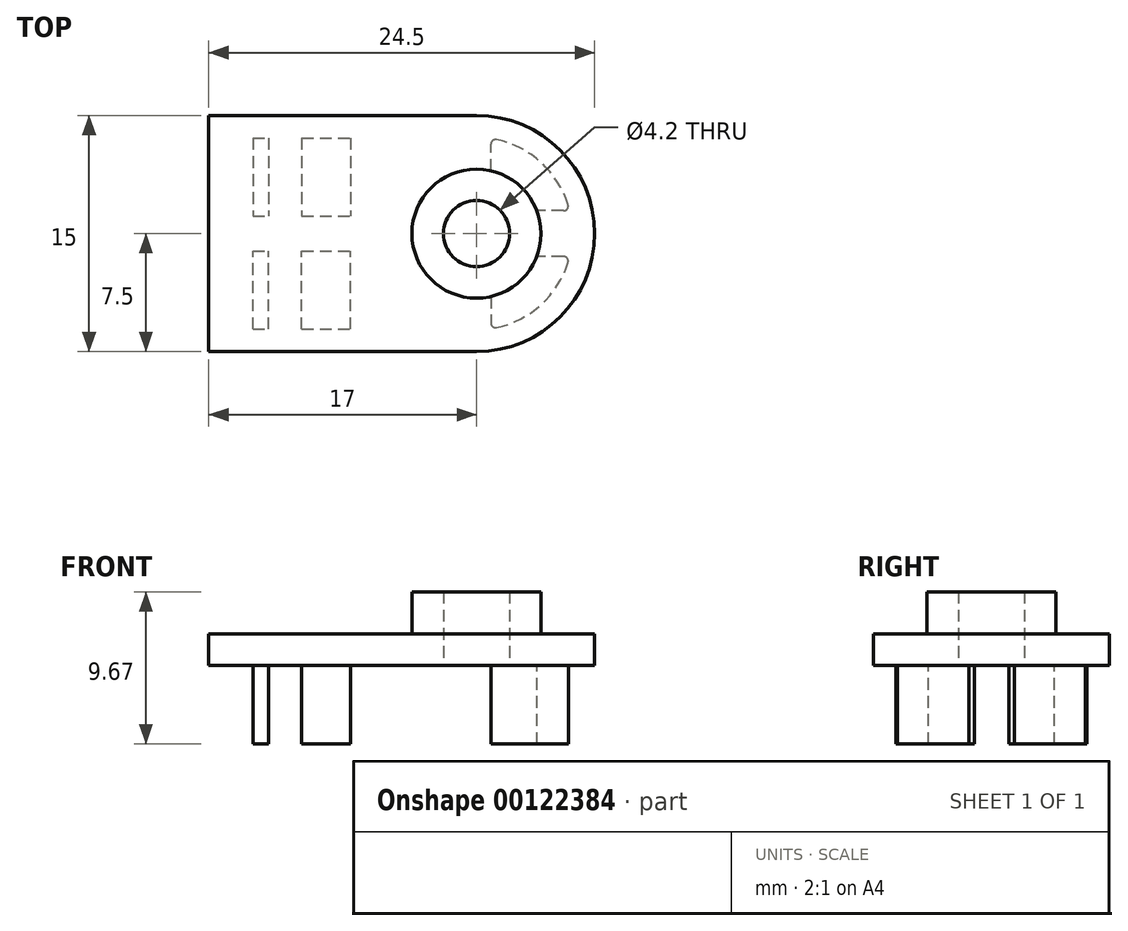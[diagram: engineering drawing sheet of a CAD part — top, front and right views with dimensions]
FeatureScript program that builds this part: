
annotation { "Feature Type Name" : "Feature", "Feature Type Description" : "" }
export const myFeature = defineFeature(function(context is Context, id is Id, definition is map)
    precondition{}
    {
        {
            var Q0;
            Q0=qCreatedBy(makeId("Top.planeOp"),FACE);
            var sketch = newSketch(context, id + "F0", { "sketchPlane" : qUnion([Q0])});
            skLineSegment(sketch, "E0.bottom", {"start": v(0, 0) * mm, "end": v(17, 0) * mm});
            skLineSegment(sketch, "E0.top", {"start": v(0, 15) * mm, "end": v(17, 15) * mm});
            skLineSegment(sketch, "E0.left", {"start": v(0, 0) * mm, "end": v(0, 15) * mm});
            skLineSegment(sketch, "E0.right", {"start": v(17, 0) * mm, "end": v(17, 15) * mm, "construction": true});
            skArc(sketch, "E1", {"start": v(17, 0) * mm, "mid": v(24.5, 7.5) * mm, "end": v(17, 15) * mm});
            skCircle(sketch, "E2", {"center": v(17, 7.5) * mm, "radius": 2.1 * mm});
            skSolve(sketch);
        }
        {
            var Q0;
            Q0 = qSketchRegion(id + "F0", true);
            extrude(context, id + "F1", {"entities" : qUnion([Q0]), "depth" : 2 * mm});
        }
        {
            var Q0;
            Q0=makeQuery(id+"F1.opExtrude","CAP_FACE",FACE,{"disambiguationData":[OSD([sQuery(id+"F0.wireOp",EDGE,"E0.bottom"),sQuery(id+"F0.wireOp",EDGE,"E0.top"),sQuery(id+"F0.wireOp",EDGE,"E0.left"),sQuery(id+"F0.wireOp",EDGE,"E1"),sQuery(id+"F0.wireOp",EDGE,"E2")])],"isStart":false});
            var sketch = newSketch(context, id + "F2", { "sketchPlane" : qUnion([Q0])});
            skCircle(sketch, "E3", {"center": v(17, 7.5) * mm, "radius": 4.1 * mm});
            skCircle(sketch, "E4", {"center": v(17, 7.5) * mm, "radius": 2.1 * mm});
            skSolve(sketch);
        }
        {
            var Q0;
            Q0=makeQuery(id+"F2.imprint","IMPRINT",FACE,{"disambiguationData":[TD([[makeQuery(id+"F2.imprint","IMPRINT",EDGE,{"derivedFrom":sQuery(id+"F2.wireOp",EDGE,"E3")}),1.0]])]});
            extrude(context, id + "F3", {"entities" : qUnion([Q0]), "operationType" : NewBodyOperationType.ADD, "depth" : 2.67 * mm});
        }
        {
            var Q0;
            Q0=makeQuery(id+"F1.opExtrude","CAP_FACE",FACE,{"disambiguationData":[OSD([sQuery(id+"F0.wireOp",EDGE,"E0.bottom"),sQuery(id+"F0.wireOp",EDGE,"E0.top"),sQuery(id+"F0.wireOp",EDGE,"E0.left"),sQuery(id+"F0.wireOp",EDGE,"E1"),sQuery(id+"F0.wireOp",EDGE,"E2")])],"isStart":true});
            var sketch = newSketch(context, id + "F4", { "sketchPlane" : qUnion([Q0])});
            skLineSegment(sketch, "E5.0", {"start": v(2.8, -1.43) * mm, "end": v(3.8, -1.43) * mm});
            skLineSegment(sketch, "E6", {"start": v(2.8, -1.43) * mm, "end": v(2.8, -6.4) * mm});
            skLineSegment(sketch, "E7", {"start": v(3.8, -1.43) * mm, "end": v(3.8, -6.4) * mm});
            skLineSegment(sketch, "E8", {"start": v(5.9, -1.43) * mm, "end": v(5.9, -6.4) * mm});
            skLineSegment(sketch, "E9", {"start": v(9, -1.43) * mm, "end": v(9, -6.4) * mm});
            skLineSegment(sketch, "E10", {"start": v(0, -7.5) * mm, "end": v(17, -7.5) * mm, "construction": true});
            skLineSegment(sketch, "E11", {"start": v(2.8, -6.4) * mm, "end": v(3.8, -6.4) * mm});
            skLineSegment(sketch, "E12.trimOffspring", {"start": v(5.9, -6.4) * mm, "end": v(9, -6.4) * mm});
            skLineSegment(sketch, "E13.trimOffspring", {"start": v(5.9, -1.43) * mm, "end": v(9, -1.43) * mm});
            skArc(sketch, "E14", {"start": v(22.82, -5.66) * mm, "mid": v(21.1, -2.99) * mm, "end": v(18.28, -1.54) * mm});
            skLineSegment(sketch, "E15", {"start": v(22.53, -6.05) * mm, "end": v(20.84, -6.05) * mm});
            skPoint(sketch, "E16.visualSharp", {"position": v(22.93, -6.05) * mm});
            skArc(sketch, "E16.filletArc", {"start": v(22.53, -6.05) * mm, "mid": v(22.77, -5.93) * mm, "end": v(22.82, -5.66) * mm});
            skArc(sketch, "E17", {"start": v(20.84, -6.05) * mm, "mid": v(19.7, -4.41) * mm, "end": v(17.92, -3.5) * mm});
            skLineSegment(sketch, "E18", {"start": v(17, -7.5) * mm, "end": v(17, -7.5) * mm});
            skLineSegment(sketch, "E19", {"start": v(22.82, -5.66) * mm, "end": v(22.82, -7.5) * mm, "construction": true});
            skLineSegment(sketch, "E20", {"start": v(22.82, -7.5) * mm, "end": v(17, -7.5) * mm, "construction": true});
            skLineSegment(sketch, "E21", {"start": v(17.92, -3.5) * mm, "end": v(17.92, -1.83) * mm});
            skPoint(sketch, "E22.visualSharp", {"position": v(17.92, -1.47) * mm});
            skArc(sketch, "E22.filletArc", {"start": v(18.28, -1.54) * mm, "mid": v(18.03, -1.6) * mm, "end": v(17.92, -1.83) * mm});
            skArc(sketch, "E23.MirrorCS", {"start": v(18.28, -13.46) * mm, "mid": v(18.03, -13.4) * mm, "end": v(17.92, -13.17) * mm});
            skArc(sketch, "E24.MirrorCS", {"start": v(22.53, -8.95) * mm, "mid": v(22.77, -9.07) * mm, "end": v(22.82, -9.34) * mm});
            skLineSegment(sketch, "E25.MirrorCS", {"start": v(2.8, -13.58) * mm, "end": v(2.8, -8.6) * mm});
            skLineSegment(sketch, "E26.MirrorCS", {"start": v(2.8, -13.58) * mm, "end": v(3.8, -13.58) * mm});
            skLineSegment(sketch, "E27.MirrorCS", {"start": v(3.8, -13.58) * mm, "end": v(3.8, -8.6) * mm});
            skLineSegment(sketch, "E28.MirrorCS", {"start": v(5.9, -8.6) * mm, "end": v(9, -8.6) * mm});
            skLineSegment(sketch, "E29.MirrorCS", {"start": v(2.8, -8.6) * mm, "end": v(3.8, -8.6) * mm});
            skLineSegment(sketch, "E30.MirrorCS", {"start": v(22.53, -8.95) * mm, "end": v(20.84, -8.95) * mm});
            skLineSegment(sketch, "E31.MirrorCS", {"start": v(5.9, -13.58) * mm, "end": v(5.9, -8.6) * mm});
            skArc(sketch, "E32.MirrorCS", {"start": v(20.84, -8.95) * mm, "mid": v(19.7, -10.59) * mm, "end": v(17.92, -11.5) * mm});
            skLineSegment(sketch, "E33.MirrorCS", {"start": v(5.9, -13.58) * mm, "end": v(9, -13.58) * mm});
            skArc(sketch, "E34.MirrorCS", {"start": v(22.82, -9.34) * mm, "mid": v(21.1, -12.01) * mm, "end": v(18.28, -13.46) * mm});
            skPoint(sketch, "E35.MirrorP", {"position": v(22.93, -8.95) * mm});
            skPoint(sketch, "E36.MirrorP", {"position": v(17.92, -13.53) * mm});
            skLineSegment(sketch, "E37.MirrorCS", {"start": v(9, -13.58) * mm, "end": v(9, -8.6) * mm});
            skLineSegment(sketch, "E38.MirrorCS", {"start": v(17.92, -11.5) * mm, "end": v(17.92, -13.17) * mm});
            skSolve(sketch);
        }
        {
            var Q0;
            Q0 = qSketchRegion(id + "F4", true);
            extrude(context, id + "F5", {"entities" : qUnion([Q0]), "operationType" : NewBodyOperationType.ADD, "depth" : 5 * mm});
        }
    });
